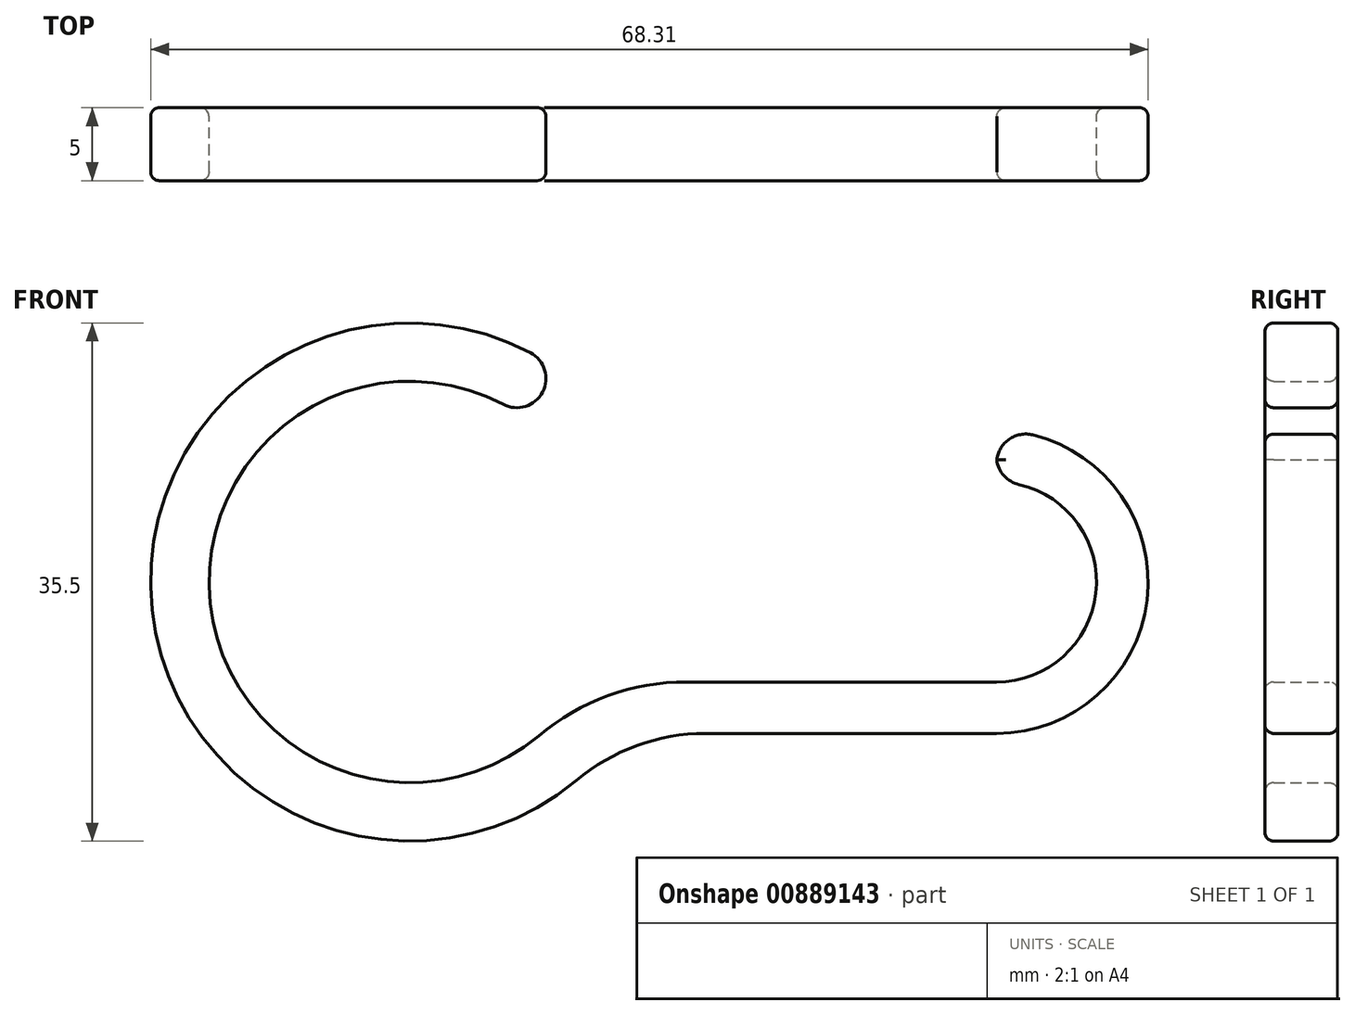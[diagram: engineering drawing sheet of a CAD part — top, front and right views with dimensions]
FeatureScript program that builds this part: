
annotation { "Feature Type Name" : "Feature", "Feature Type Description" : "" }
export const myFeature = defineFeature(function(context is Context, id is Id, definition is map)
    precondition{}
    {
        {
            var Q0;
            Q0=qCreatedBy(makeId("Front.planeOp"),FACE);
            var sketch = newSketch(context, id + "F0", { "sketchPlane" : qUnion([Q0])});
            skArc(sketch, "E0", {"start": v(7.89, 11.26) * mm, "mid": v(-13.74, -0.6) * mm, "end": v(8.84, -10.53) * mm});
            skArc(sketch, "E1", {"start": v(10.18, 14.54) * mm, "mid": v(-17.73, -0.77) * mm, "end": v(11.4, -13.6) * mm});
            skLineSegment(sketch, "E2", {"start": v(0, 0) * mm, "end": v(11.01, 15.73) * mm, "construction": true});
            skLineSegment(sketch, "E3", {"start": v(7.89, 11.26) * mm, "end": v(10.18, 14.54) * mm});
            skArc(sketch, "E4", {"start": v(20.25, -10.38) * mm, "mid": v(15.55, -11.2) * mm, "end": v(11.4, -13.6) * mm});
            skLineSegment(sketch, "E5", {"start": v(0, 0) * mm, "end": v(11.4, -13.6) * mm, "construction": true});
            skArc(sketch, "E6", {"start": v(18.96, -6.85) * mm, "mid": v(13.58, -7.8) * mm, "end": v(8.84, -10.53) * mm});
            skLineSegment(sketch, "E7", {"start": v(-1.72, -6.85) * mm, "end": v(18.96, -6.85) * mm, "construction": true});
            skLineSegment(sketch, "E8", {"start": v(-6.38, -10.38) * mm, "end": v(20.25, -10.38) * mm, "construction": true});
            skLineSegment(sketch, "E9", {"start": v(20.25, -10.38) * mm, "end": v(40.18, -10.38) * mm});
            skLineSegment(sketch, "E10", {"start": v(18.96, -6.85) * mm, "end": v(40.18, -6.85) * mm});
            skArc(sketch, "E11", {"start": v(40.18, -10.38) * mm, "mid": v(50.56, 0) * mm, "end": v(40.18, 10.38) * mm});
            skArc(sketch, "E12", {"start": v(40.18, -6.85) * mm, "mid": v(47.03, 0) * mm, "end": v(40.18, 6.85) * mm});
            skLineSegment(sketch, "E13", {"start": v(40.18, 6.85) * mm, "end": v(40.18, 10.38) * mm});
            skSolve(sketch);
        }
        {
            var Q0;
            Q0 = qSketchRegion(id + "F0", true);
            extrude(context, id + "F1", {"entities" : qUnion([Q0]), "depth" : 5 * mm, "offsetDistance" : 25 * mm});
        }
        {
            var Q0;
            Q0=makeQuery(id+"F1.opExtrude","SWEPT_EDGE",EDGE,{"disambiguationData":[OSD([sQuery(id+"F0.wireOp",EDGE,"E0"),sQuery(id+"F0.wireOp",EDGE,"E3")])]});
            var Q1;
            Q1=makeQuery(id+"F1.opExtrude","SWEPT_EDGE",EDGE,{"disambiguationData":[OSD([sQuery(id+"F0.wireOp",EDGE,"E1"),sQuery(id+"F0.wireOp",EDGE,"E3")])]});
            var Q2;
            Q2=makeQuery(id+"F1.opExtrude","SWEPT_EDGE",EDGE,{"disambiguationData":[OSD([sQuery(id+"F0.wireOp",EDGE,"E11"),sQuery(id+"F0.wireOp",EDGE,"E13")])]});
            var Q3;
            Q3=makeQuery(id+"F1.opExtrude","SWEPT_EDGE",EDGE,{"disambiguationData":[OSD([sQuery(id+"F0.wireOp",EDGE,"E12"),sQuery(id+"F0.wireOp",EDGE,"E13")])]});
            fillet(context, id + "F2", {"entities" : qUnion([Q0, Q1, Q2, Q3]), "radius" : 2 * mm, "tangentPropagation" : true, "allowEdgeOverflow" : false});
        }
        {
            var Q0;
            Q0=makeQuery(id+"F1.opExtrude","CAP_EDGE",EDGE,{"disambiguationData":[OSD([sQuery(id+"F0.wireOp",EDGE,"E1")])],"isStart":false});
            var Q1;
            Q1=makeQuery(id+"F1.opExtrude","CAP_FACE",FACE,{"disambiguationData":[OSD([sQuery(id+"F0.wireOp",EDGE,"E0"),sQuery(id+"F0.wireOp",EDGE,"E1"),sQuery(id+"F0.wireOp",EDGE,"E3"),sQuery(id+"F0.wireOp",EDGE,"E4"),sQuery(id+"F0.wireOp",EDGE,"E6"),sQuery(id+"F0.wireOp",EDGE,"E9"),sQuery(id+"F0.wireOp",EDGE,"E10"),sQuery(id+"F0.wireOp",EDGE,"E11"),sQuery(id+"F0.wireOp",EDGE,"E12"),sQuery(id+"F0.wireOp",EDGE,"E13")])],"isStart":true});
            fillet(context, id + "F3", {"entities" : qUnion([Q0, Q1]), "radius" : 0.6 * mm, "tangentPropagation" : true, "allowEdgeOverflow" : false});
        }
    });
